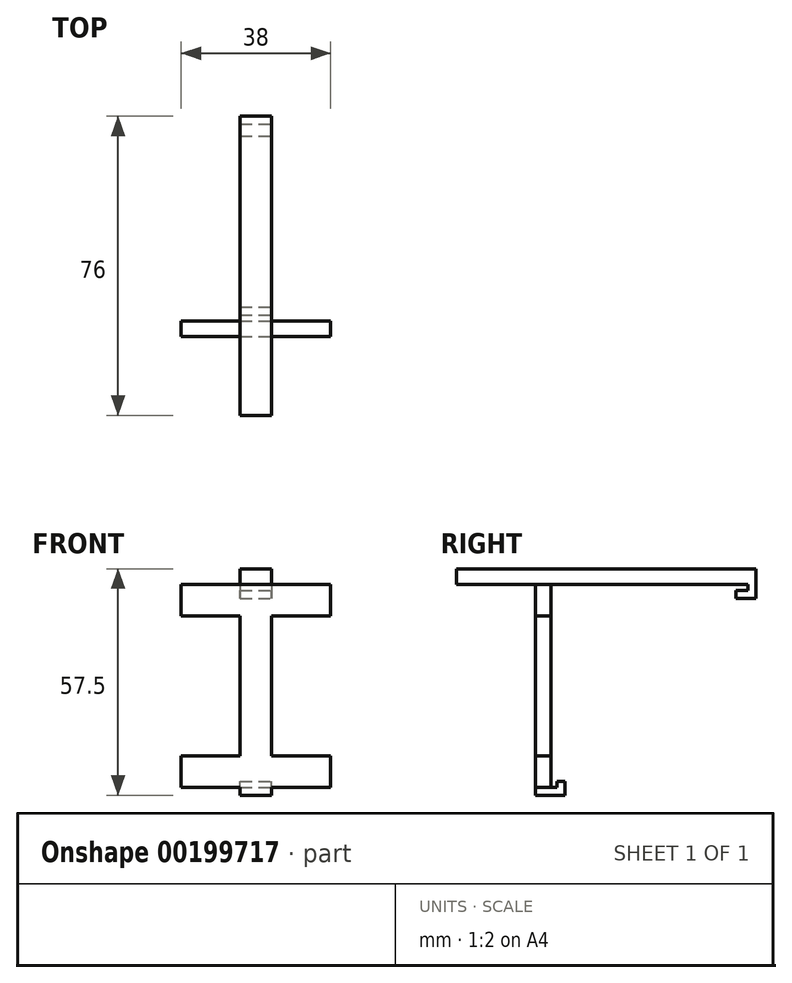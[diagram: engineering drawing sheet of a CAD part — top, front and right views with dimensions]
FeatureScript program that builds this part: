
annotation { "Feature Type Name" : "Feature", "Feature Type Description" : "" }
export const myFeature = defineFeature(function(context is Context, id is Id, definition is map)
    precondition{}
    {
        {
            var Q0;
            Q0=qCreatedBy(makeId("Front.planeOp"),FACE);
            var sketch = newSketch(context, id + "F0", { "sketchPlane" : qUnion([Q0])});
            skLineSegment(sketch, "E0.bottom", {"start": v(0, 0) * mm, "end": v(8, 0) * mm});
            skLineSegment(sketch, "E0.top", {"start": v(0, 53.5) * mm, "end": v(8, 53.5) * mm});
            skLineSegment(sketch, "E0.left", {"start": v(0, 0) * mm, "end": v(0, 53.5) * mm});
            skLineSegment(sketch, "E0.right", {"start": v(8, 0) * mm, "end": v(8, 53.5) * mm});
            skSolve(sketch);
        }
        {
            var Q0;
            Q0=makeQuery(id+"F0.imprint","IMPRINT",FACE,{"disambiguationData":[TD([[makeQuery(id+"F0.imprint","IMPRINT",EDGE,{"derivedFrom":sQuery(id+"F0.wireOp",EDGE,"E0.bottom")}),1.0]])]});
            extrude(context, id + "F1", {"entities" : qUnion([Q0]), "depth" : 4 * mm});
        }
        {
            var Q0;
            Q0=makeQuery(id+"F1.opExtrude","SWEPT_FACE",FACE,{"disambiguationData":[OSD([sQuery(id+"F0.wireOp",EDGE,"E0.top")])]});
            var sketch = newSketch(context, id + "F2", { "sketchPlane" : qUnion([Q0])});
            skLineSegment(sketch, "E1.bottom", {"start": v(0, -4) * mm, "end": v(8, -4) * mm});
            skLineSegment(sketch, "E1.top", {"start": v(0, 52) * mm, "end": v(8, 52) * mm});
            skLineSegment(sketch, "E1.left", {"start": v(0, -4) * mm, "end": v(0, 52) * mm});
            skLineSegment(sketch, "E1.right", {"start": v(8, -4) * mm, "end": v(8, 52) * mm});
            skSolve(sketch);
        }
        {
            var Q0;
            {var subQ0=sQuery(id+"F2.wireOp",EDGE,"E1.top");Q0=makeQuery(id+"F2.imprint","IMPRINT",FACE,{"disambiguationData":[TD([[makeQuery(id+"F2.imprint","IMPRINT",EDGE,{"derivedFrom":subQ0}),-1.0]])]});}
            var Q1;
            {var subQ0=sQuery(id+"F2.wireOp",EDGE,"E1.bottom");Q1=makeQuery(id+"F2.imprint","IMPRINT",FACE,{"disambiguationData":[TD([[makeQuery(id+"F2.imprint","IMPRINT",EDGE,{"derivedFrom":subQ0}),1.0]])]});}
            extrude(context, id + "F3", {"entities" : qUnion([Q0, Q1]), "operationType" : NewBodyOperationType.ADD, "depth" : 4 * mm});
        }
        {
            var Q0;
            Q0=makeQuery(id+"F3.boolean.opBoolean","MERGE",FACE,{"derivedFrom":[makeQuery(id+"F1.opExtrude","SWEPT_FACE",FACE,{"disambiguationData":[OSD([sQuery(id+"F0.wireOp",EDGE,"E0.right")])]}),makeQuery(id+"F3.opExtrude","SWEPT_FACE",FACE,{"disambiguationData":[OSD([sQuery(id+"F2.wireOp",EDGE,"E1.right")])]})]});
            var sketch = newSketch(context, id + "F4", { "sketchPlane" : qUnion([Q0])});
            skLineSegment(sketch, "E2.bottom", {"start": v(52, 53.5) * mm, "end": v(50, 53.5) * mm});
            skLineSegment(sketch, "E2.top", {"start": v(52, 50) * mm, "end": v(50, 50) * mm});
            skLineSegment(sketch, "E2.left", {"start": v(52, 53.5) * mm, "end": v(52, 50) * mm});
            skLineSegment(sketch, "E2.right", {"start": v(50, 53.5) * mm, "end": v(50, 52) * mm});
            skLineSegment(sketch, "E3.bottom", {"start": v(50, 50) * mm, "end": v(47, 50) * mm});
            skLineSegment(sketch, "E3.top", {"start": v(50, 52) * mm, "end": v(47, 52) * mm});
            skLineSegment(sketch, "E3.right", {"start": v(47, 50) * mm, "end": v(47, 52) * mm});
            skSolve(sketch);
        }
        {
            var Q0;
            Q0=makeQuery(id+"F4.imprint","IMPRINT",FACE,{"disambiguationData":[TD([[makeQuery(id+"F4.imprint","IMPRINT",EDGE,{"derivedFrom":sQuery(id+"F4.wireOp",EDGE,"E2.bottom")}),-1.0]])]});
            extrude(context, id + "F5", {"entities" : qUnion([Q0]), "operationType" : NewBodyOperationType.ADD, "oppositeDirection" : true, "depth" : 8 * mm});
        }
        {
            var Q0;
            Q0=makeQuery(id+"F5.boolean.opBoolean","MERGE",FACE,{"derivedFrom":[makeQuery(id+"F3.boolean.opBoolean","MERGE",FACE,{"derivedFrom":[makeQuery(id+"F1.opExtrude","SWEPT_FACE",FACE,{"disambiguationData":[OSD([sQuery(id+"F0.wireOp",EDGE,"E0.right")])]}),makeQuery(id+"F3.opExtrude","SWEPT_FACE",FACE,{"disambiguationData":[OSD([sQuery(id+"F2.wireOp",EDGE,"E1.right")])]})]}),makeQuery(id+"F5.opExtrude","CAP_FACE",FACE,{"disambiguationData":[OSD([sQuery(id+"F4.wireOp",EDGE,"E2.bottom"),sQuery(id+"F4.wireOp",EDGE,"E2.top"),sQuery(id+"F4.wireOp",EDGE,"E2.left"),sQuery(id+"F4.wireOp",EDGE,"E2.right"),sQuery(id+"F4.wireOp",EDGE,"E3.bottom"),sQuery(id+"F4.wireOp",EDGE,"E3.top"),sQuery(id+"F4.wireOp",EDGE,"E3.right")])],"isStart":true})]});
            var sketch = newSketch(context, id + "F6", { "sketchPlane" : qUnion([Q0])});
            skLineSegment(sketch, "E4.bottom", {"start": v(0, 0) * mm, "end": v(3.5, 0) * mm});
            skLineSegment(sketch, "E4.top", {"start": v(0, 2) * mm, "end": v(1.5, 2) * mm});
            skLineSegment(sketch, "E4.left", {"start": v(0, 0) * mm, "end": v(0, 2) * mm});
            skLineSegment(sketch, "E4.right", {"start": v(3.5, 0) * mm, "end": v(3.5, 2) * mm});
            skLineSegment(sketch, "E5.top", {"start": v(3.5, 3.5) * mm, "end": v(1.5, 3.5) * mm});
            skLineSegment(sketch, "E5.left", {"start": v(3.5, 2) * mm, "end": v(3.5, 3.5) * mm});
            skLineSegment(sketch, "E5.right", {"start": v(1.5, 2) * mm, "end": v(1.5, 3.5) * mm});
            skSolve(sketch);
        }
        {
            var Q0;
            Q0=makeQuery(id+"F6.imprint","IMPRINT",FACE,{"disambiguationData":[TD([[makeQuery(id+"F6.imprint","IMPRINT",EDGE,{"derivedFrom":sQuery(id+"F6.wireOp",EDGE,"E4.bottom")}),1.0]])]});
            extrude(context, id + "F7", {"entities" : qUnion([Q0]), "oppositeDirection" : true, "depth" : 8 * mm});
        }
        {
            var Q0;
            Q0=makeQuery(id+"F1.opExtrude","SWEPT_BODY",BODY,{"disambiguationData":[OSD([sQuery(id+"F0.wireOp",EDGE,"E0.bottom"),sQuery(id+"F0.wireOp",EDGE,"E0.top"),sQuery(id+"F0.wireOp",EDGE,"E0.left"),sQuery(id+"F0.wireOp",EDGE,"E0.right")])]});
            var Q1;
            Q1=makeQuery(id+"F7.opExtrude","SWEPT_BODY",BODY,{"disambiguationData":[OSD([sQuery(id+"F6.wireOp",EDGE,"E4.bottom"),sQuery(id+"F6.wireOp",EDGE,"E4.top"),sQuery(id+"F6.wireOp",EDGE,"E4.left"),sQuery(id+"F6.wireOp",EDGE,"E4.right"),sQuery(id+"F6.wireOp",EDGE,"E5.top"),sQuery(id+"F6.wireOp",EDGE,"E5.left"),sQuery(id+"F6.wireOp",EDGE,"E5.right")])]});
            booleanBodies(context, id + "F8", {"operationType" : BooleanOperationType.UNION, "tools" : qUnion([Q0, Q1])});
        }
        {
            var Q0;
            Q0=makeQuery(id+"F3.boolean.opBoolean","MERGE",FACE,{"derivedFrom":[makeQuery(id+"F1.opExtrude","CAP_FACE",FACE,{"disambiguationData":[OSD([sQuery(id+"F0.wireOp",EDGE,"E0.bottom"),sQuery(id+"F0.wireOp",EDGE,"E0.top"),sQuery(id+"F0.wireOp",EDGE,"E0.left"),sQuery(id+"F0.wireOp",EDGE,"E0.right")])],"isStart":false}),makeQuery(id+"F3.opExtrude","SWEPT_FACE",FACE,{"disambiguationData":[OSD([sQuery(id+"F2.wireOp",EDGE,"E1.bottom")])]})]});
            var sketch = newSketch(context, id + "F9", { "sketchPlane" : qUnion([Q0])});
            skLineSegment(sketch, "E6.bottom", {"start": v(0, 57.5) * mm, "end": v(8, 57.5) * mm});
            skLineSegment(sketch, "E6.top", {"start": v(0, 53.5) * mm, "end": v(8, 53.5) * mm});
            skLineSegment(sketch, "E6.left", {"start": v(0, 57.5) * mm, "end": v(0, 53.5) * mm});
            skLineSegment(sketch, "E6.right", {"start": v(8, 57.5) * mm, "end": v(8, 53.5) * mm});
            skSolve(sketch);
        }
        {
            var Q0;
            Q0 = qSketchRegion(id + "F9", true);
            extrude(context, id + "F10", {"entities" : qUnion([Q0]), "operationType" : NewBodyOperationType.ADD, "depth" : 20 * mm});
        }
        {
            var Q0;
            Q0=makeQuery(id+"F10.boolean.opBoolean","MERGE",FACE,{"derivedFrom":[makeQuery(id+"F8.opBoolean","MERGE",FACE,{"derivedFrom":[makeQuery(id+"F5.boolean.opBoolean","MERGE",FACE,{"derivedFrom":[makeQuery(id+"F3.boolean.opBoolean","MERGE",FACE,{"derivedFrom":[makeQuery(id+"F1.opExtrude","SWEPT_FACE",FACE,{"disambiguationData":[OSD([sQuery(id+"F0.wireOp",EDGE,"E0.right")])]}),makeQuery(id+"F3.opExtrude","SWEPT_FACE",FACE,{"disambiguationData":[OSD([sQuery(id+"F2.wireOp",EDGE,"E1.right")])]})]}),makeQuery(id+"F5.opExtrude","CAP_FACE",FACE,{"disambiguationData":[OSD([sQuery(id+"F4.wireOp",EDGE,"E2.bottom"),sQuery(id+"F4.wireOp",EDGE,"E2.top"),sQuery(id+"F4.wireOp",EDGE,"E2.left"),sQuery(id+"F4.wireOp",EDGE,"E2.right"),sQuery(id+"F4.wireOp",EDGE,"E3.bottom"),sQuery(id+"F4.wireOp",EDGE,"E3.top"),sQuery(id+"F4.wireOp",EDGE,"E3.right")])],"isStart":true})]}),makeQuery(id+"F7.opExtrude","CAP_FACE",FACE,{"disambiguationData":[OSD([sQuery(id+"F6.wireOp",EDGE,"E4.bottom"),sQuery(id+"F6.wireOp",EDGE,"E4.top"),sQuery(id+"F6.wireOp",EDGE,"E4.left"),sQuery(id+"F6.wireOp",EDGE,"E4.right"),sQuery(id+"F6.wireOp",EDGE,"E5.top"),sQuery(id+"F6.wireOp",EDGE,"E5.left"),sQuery(id+"F6.wireOp",EDGE,"E5.right")])],"isStart":true})]}),makeQuery(id+"F10.opExtrude","SWEPT_FACE",FACE,{"disambiguationData":[OSD([sQuery(id+"F9.wireOp",EDGE,"E6.right")])]})]});
            var sketch = newSketch(context, id + "F11", { "sketchPlane" : qUnion([Q0])});
            skLineSegment(sketch, "E7.bottom", {"start": v(-4, 53.5) * mm, "end": v(0, 53.5) * mm});
            skLineSegment(sketch, "E7.top", {"start": v(-4, 45.5) * mm, "end": v(0, 45.5) * mm});
            skLineSegment(sketch, "E7.left", {"start": v(-4, 53.5) * mm, "end": v(-4, 45.5) * mm});
            skLineSegment(sketch, "E7.right", {"start": v(0, 53.5) * mm, "end": v(0, 45.5) * mm});
            skLineSegment(sketch, "E8.bottom", {"start": v(0, 2) * mm, "end": v(-4, 2) * mm});
            skLineSegment(sketch, "E8.top", {"start": v(0, 10) * mm, "end": v(-4, 10) * mm});
            skLineSegment(sketch, "E8.left", {"start": v(0, 2) * mm, "end": v(0, 10) * mm});
            skLineSegment(sketch, "E8.right", {"start": v(-4, 2) * mm, "end": v(-4, 10) * mm});
            skSolve(sketch);
        }
        {
            var Q0;
            Q0=makeQuery(id+"F11.imprint","IMPRINT",FACE,{"disambiguationData":[TD([[makeQuery(id+"F11.imprint","IMPRINT",EDGE,{"derivedFrom":sQuery(id+"F11.wireOp",EDGE,"E7.bottom")}),-1.0]])]});
            var Q1;
            Q1=makeQuery(id+"F11.imprint","IMPRINT",FACE,{"disambiguationData":[TD([[makeQuery(id+"F11.imprint","IMPRINT",EDGE,{"derivedFrom":sQuery(id+"F11.wireOp",EDGE,"E8.bottom")}),-1.0]])]});
            extrude(context, id + "F12", {"entities" : qUnion([Q0, Q1]), "operationType" : NewBodyOperationType.ADD, "depth" : 15 * mm, "hasSecondDirection" : true, "secondDirectionOppositeDirection" : true, "secondDirectionDepth" : 23 * mm});
        }
    });
